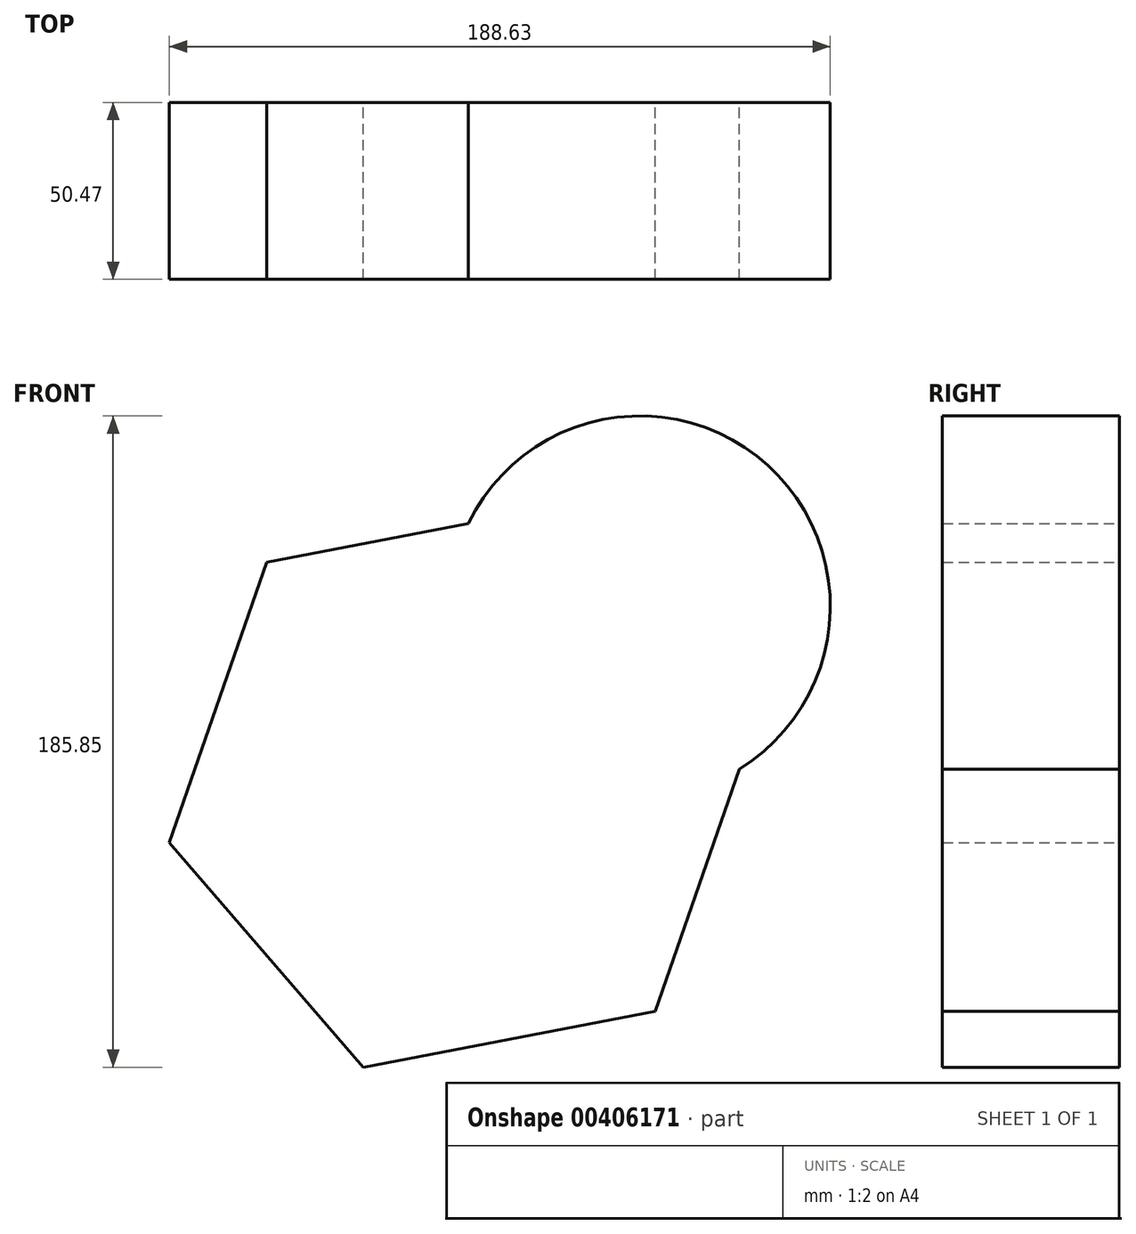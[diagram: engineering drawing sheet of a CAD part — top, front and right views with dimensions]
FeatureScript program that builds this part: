
annotation { "Feature Type Name" : "Feature", "Feature Type Description" : "" }
export const myFeature = defineFeature(function(context is Context, id is Id, definition is map)
    precondition{}
    {
        {
            var Q0;
            Q0=qCreatedBy(makeId("Front.planeOp"),FACE);
            var sketch = newSketch(context, id + "F0", { "sketchPlane" : qUnion([Q0])});
            skCircle(sketch, "E0", {"center": v(0, 15.77) * mm, "radius": 54.38 * mm});
            skCircle(sketch, "E1.cCircle", {"center": v(-51.03, -35.68) * mm, "radius": 84.72 * mm, "construction": true});
            skLineSegment(sketch, "E1.0", {"start": v(-106.43, 28.42) * mm, "end": v(-23.21, 44.34) * mm});
            skLineSegment(sketch, "E1.1", {"start": v(-23.21, 44.34) * mm, "end": v(32.18, -19.76) * mm});
            skLineSegment(sketch, "E1.2", {"start": v(32.18, -19.76) * mm, "end": v(4.36, -99.79) * mm});
            skLineSegment(sketch, "E1.3", {"start": v(4.36, -99.79) * mm, "end": v(-78.85, -115.7) * mm});
            skLineSegment(sketch, "E1.4", {"start": v(-78.85, -115.7) * mm, "end": v(-134.25, -51.6) * mm});
            skLineSegment(sketch, "E1.5", {"start": v(-134.25, -51.6) * mm, "end": v(-106.43, 28.42) * mm});
            skSolve(sketch);
        }
        {
            var Q0;
            Q0 = qSketchRegion(id + "F0", true);
            extrude(context, id + "F1", {"entities" : qUnion([Q0]), "depth" : 50.47 * mm});
        }
    });
